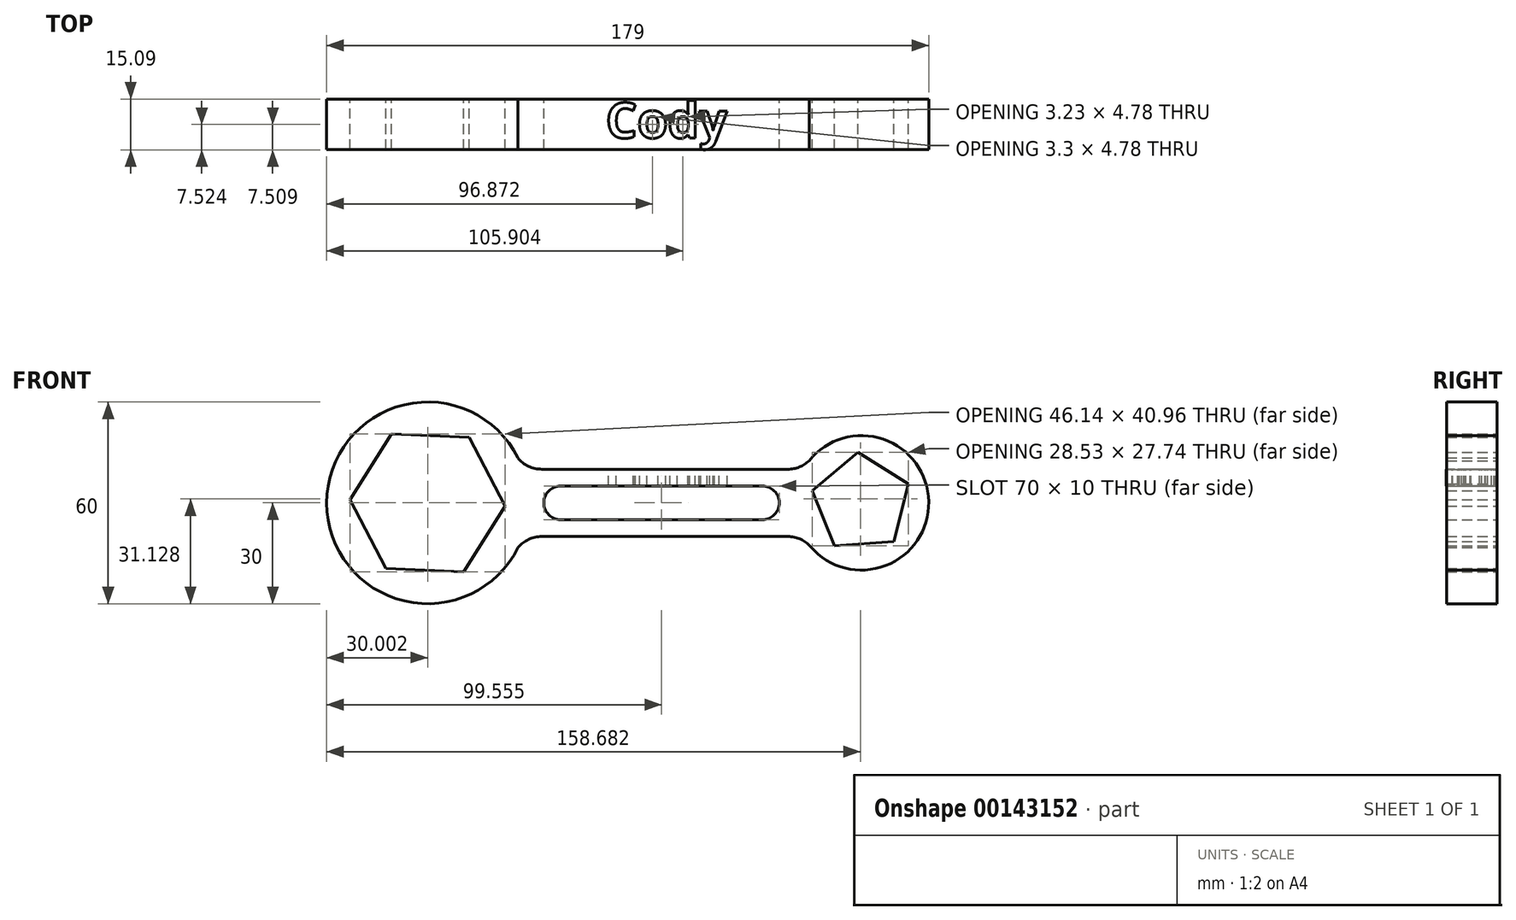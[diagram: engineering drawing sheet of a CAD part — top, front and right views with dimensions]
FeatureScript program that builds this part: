
annotation { "Feature Type Name" : "Feature", "Feature Type Description" : "" }
export const myFeature = defineFeature(function(context is Context, id is Id, definition is map)
    precondition{}
    {
        {
            var Q0;
            Q0=qCreatedBy(makeId("Front.planeOp"),FACE);
            var sketch = newSketch(context, id + "F0", { "sketchPlane" : qUnion([Q0])});
            skCircle(sketch, "E0", {"center": v(-71.49, 0) * mm, "radius": 30 * mm});
            skCircle(sketch, "E1", {"center": v(57.51, 0) * mm, "radius": 20 * mm});
            skLineSegment(sketch, "E2", {"start": v(-37.55, -10) * mm, "end": v(35.62, -10) * mm});
            skLineSegment(sketch, "E3", {"start": v(-37.55, 10) * mm, "end": v(35.62, 10) * mm});
            skLineSegment(sketch, "E4", {"start": v(-31.93, 5) * mm, "end": v(28.07, 5) * mm});
            skLineSegment(sketch, "E5", {"start": v(-31.93, -5) * mm, "end": v(28.07, -5) * mm});
            skArc(sketch, "E6", {"start": v(-31.93, 5) * mm, "mid": v(-36.93, 0) * mm, "end": v(-31.93, -5) * mm});
            skArc(sketch, "E7", {"start": v(28.07, 5) * mm, "mid": v(33.07, 0) * mm, "end": v(28.07, -5) * mm});
            skCircle(sketch, "E8.cCircle", {"center": v(-71.49, 0) * mm, "radius": 20 * mm, "construction": true});
            skLineSegment(sketch, "E8.0", {"start": v(-83.89, -19.48) * mm, "end": v(-94.56, 1) * mm});
            skLineSegment(sketch, "E8.1", {"start": v(-94.56, 1) * mm, "end": v(-82.16, 20.48) * mm});
            skLineSegment(sketch, "E8.2", {"start": v(-82.16, 20.48) * mm, "end": v(-59.09, 19.48) * mm});
            skLineSegment(sketch, "E8.3", {"start": v(-59.09, 19.48) * mm, "end": v(-48.42, -1) * mm});
            skLineSegment(sketch, "E8.4", {"start": v(-48.42, -1) * mm, "end": v(-60.82, -20.48) * mm});
            skLineSegment(sketch, "E8.5", {"start": v(-60.82, -20.48) * mm, "end": v(-83.89, -19.48) * mm});
            skCircle(sketch, "E9.cCircle", {"center": v(57.51, 0) * mm, "radius": 12.16 * mm, "construction": true});
            skLineSegment(sketch, "E9.0", {"start": v(56.48, 15) * mm, "end": v(71.46, 5.62) * mm});
            skLineSegment(sketch, "E9.1", {"start": v(71.46, 5.62) * mm, "end": v(67.17, -11.53) * mm});
            skLineSegment(sketch, "E9.2", {"start": v(67.17, -11.53) * mm, "end": v(49.53, -12.74) * mm});
            skLineSegment(sketch, "E9.3", {"start": v(49.53, -12.74) * mm, "end": v(42.93, 3.65) * mm});
            skLineSegment(sketch, "E9.4", {"start": v(42.93, 3.65) * mm, "end": v(56.48, 15) * mm});
            skPoint(sketch, "E9.0.midPoint", {"position": v(63.97, 10.31) * mm});
            skArc(sketch, "E10", {"start": v(-37.55, 10) * mm, "mid": v(-41.48, 10.9) * mm, "end": v(-44.64, 13.4) * mm});
            skArc(sketch, "E11", {"start": v(-37.55, -10) * mm, "mid": v(-41.43, -10.86) * mm, "end": v(-44.59, -13.28) * mm});
            skArc(sketch, "E12", {"start": v(35.62, -10) * mm, "mid": v(39.35, -10.81) * mm, "end": v(42.4, -13.1) * mm});
            skArc(sketch, "E13", {"start": v(35.62, 10) * mm, "mid": v(39.03, 10.66) * mm, "end": v(41.94, 12.55) * mm});
            skSolve(sketch);
        }
        {
            var Q0;
            Q0 = qSketchRegion(id + "F0", true);
            extrude(context, id + "F1", {"entities" : qUnion([Q0]), "depth" : 15 * mm});
        }
        {
            var Q0;
            Q0=makeQuery(id+"F1.opExtrude","SWEPT_FACE",FACE,{"disambiguationData":[OSD([sQuery(id+"F0.wireOp",EDGE,"E3")])]});
            var sketch = newSketch(context, id + "F2", { "sketchPlane" : qUnion([Q0])});
            skText(sketch, "E14", { "text": "Cody", "fontName": "OpenSans-Bold.ttf"});
            const initialGuessF2  = {"E14": [-0.0185, -0.01157, 1, 0, 0.01056]};
            skSetInitialGuess(sketch, initialGuessF2);
            skSolve(sketch);
        }
        {
            var Q0;
            Q0 = qSketchRegion(id + "F2", true);
            extrude(context, id + "F3", {"entities" : qUnion([Q0]), "oppositeDirection" : true, "depth" : 5 * mm});
        }
    });
